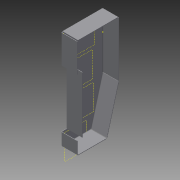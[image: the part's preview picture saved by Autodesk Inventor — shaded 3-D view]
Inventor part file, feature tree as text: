
AUTODESK INVENTOR PART (.ipt)
format: ipt  version: 2015 (Build 190159000, 159)  size: 163,840 bytes
history: native  units: mm
features: reference x8, sheet_metal_op x4, sketch x3, other x2
ambient origin geometry x8: Origin, YZ Plane, XZ Plane, XY Plane, X Axis, Y Axis, Z Axis, Center Point
bodies: Solid1 (feature_tree)
feature tree (17):
  sheet_metal_op  "Face1"
  sketch  "Sketch3"  dims[d16=320.0mm]
  sheet_metal_op  "Flange4"
  sketch  "Sketch1"  dims[d1=1.6mm]
  reference  "Reference1"
  reference  "Reference2"
  other  "Plate1"
  reference  "Reference3"
  reference  "Reference4"
  reference  "Reference5"
  reference  "Reference6"
  reference  "Reference7"
  reference  "Reference8"
  sketch  "Sketch6"  dims[d17=35.0mm d18=50.0mm d19=3.922832mm d40=5.0mm d41=48.571429mm d42=5.0mm d43=5.0mm d44=1.6mm d45=0.8mm d46=3.2mm d47=1.6mm d48=52.0mm d49=90.0deg d50=1.6mm d51=6.4mm d52=1.6mm d53=1.6mm]
  other  "Plate5"
  sheet_metal_op  "Bend4"
  sheet_metal_op  "Corner4"
